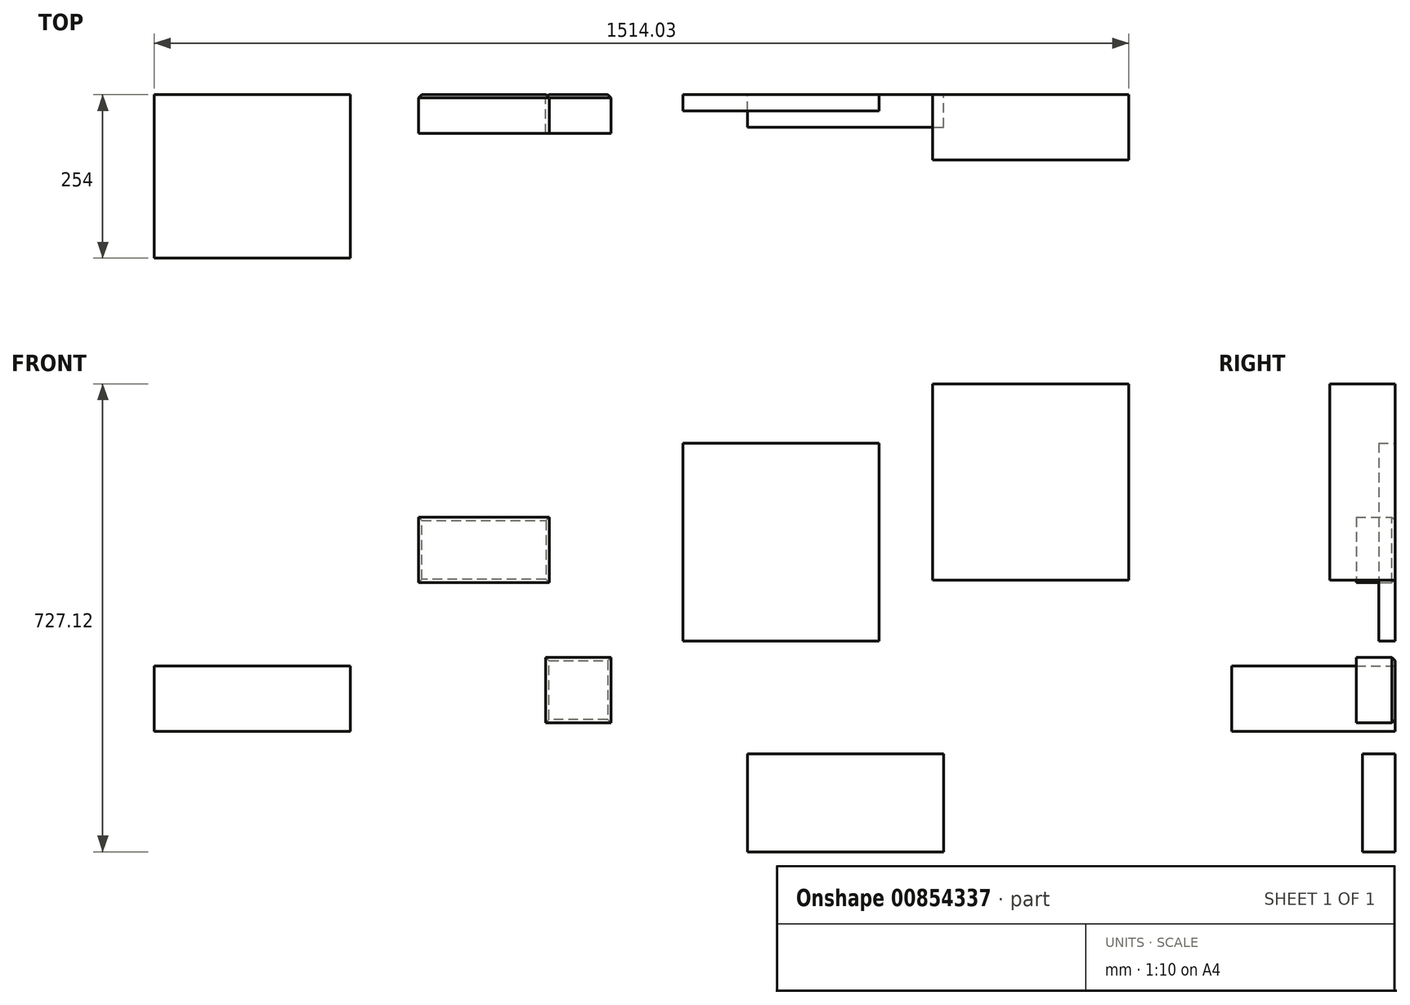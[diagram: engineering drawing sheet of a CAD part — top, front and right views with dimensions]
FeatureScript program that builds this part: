
annotation { "Feature Type Name" : "Feature", "Feature Type Description" : "" }
export const myFeature = defineFeature(function(context is Context, id is Id, definition is map)
    precondition{}
    {
        {
            var Q0;
            Q0=qCreatedBy(makeId("Front.planeOp"),FACE);
            var sketch = newSketch(context, id + "F0", { "sketchPlane" : qUnion([Q0])});
            skLineSegment(sketch, "E0.bottom", {"start": v(-238.03, 40.6) * mm, "end": v(-34.83, 40.6) * mm});
            skLineSegment(sketch, "E0.top", {"start": v(-238.03, -61) * mm, "end": v(-34.83, -61) * mm});
            skLineSegment(sketch, "E0.left", {"start": v(-238.03, 40.6) * mm, "end": v(-238.03, -61) * mm});
            skLineSegment(sketch, "E0.right", {"start": v(-34.83, 40.6) * mm, "end": v(-34.83, -61) * mm});
            skLineSegment(sketch, "E1.bottom", {"start": v(-238.03, 40.6) * mm, "end": v(-339.63, 40.6) * mm});
            skLineSegment(sketch, "E1.top", {"start": v(-238.03, -162.6) * mm, "end": v(-339.63, -162.6) * mm});
            skLineSegment(sketch, "E1.left", {"start": v(-238.03, 40.6) * mm, "end": v(-238.03, -162.6) * mm});
            skLineSegment(sketch, "E1.right", {"start": v(-339.63, 40.6) * mm, "end": v(-339.63, -162.6) * mm});
            skLineSegment(sketch, "E2.bottom", {"start": v(-238.03, -61) * mm, "end": v(-135.35, -61) * mm});
            skLineSegment(sketch, "E2.top", {"start": v(-238.03, -252.07) * mm, "end": v(-135.35, -252.07) * mm});
            skLineSegment(sketch, "E2.left", {"start": v(-238.03, -61) * mm, "end": v(-238.03, -252.07) * mm});
            skLineSegment(sketch, "E2.right", {"start": v(-135.35, -61) * mm, "end": v(-135.35, -252.07) * mm});
            skSolve(sketch);
        }
        {
            var Q0;
            Q0=makeQuery(id+"F0.imprint","IMPRINT",FACE,{"disambiguationData":[TD([[makeQuery(id+"F0.imprint","IMPRINT",EDGE,{"derivedFrom":sQuery(id+"F0.wireOp",EDGE,"E0.bottom")}),-1.0]])]});
            extrude(context, id + "F1", {"entities" : qUnion([Q0]), "depth" : 60.32 * mm, "offsetDistance" : 25.4 * mm});
        }
        {
            var Q0;
            Q0=makeQuery(id+"F1.opExtrude","CAP_EDGE",EDGE,{"disambiguationData":[OSD([sQuery(id+"F0.wireOp",EDGE,"E0.top")])],"isStart":true});
            var Q1;
            Q1=makeQuery(id+"F1.opExtrude","CAP_EDGE",EDGE,{"disambiguationData":[OSD([sQuery(id+"F0.wireOp",EDGE,"E0.left")])],"isStart":true});
            var Q2;
            Q2=makeQuery(id+"F1.opExtrude","CAP_EDGE",EDGE,{"disambiguationData":[OSD([sQuery(id+"F0.wireOp",EDGE,"E0.bottom")])],"isStart":true});
            var Q3;
            Q3=makeQuery(id+"F1.opExtrude","CAP_EDGE",EDGE,{"disambiguationData":[OSD([sQuery(id+"F0.wireOp",EDGE,"E0.right")])],"isStart":true});
            chamfer(context, id + "F2", {"entities" : qUnion([Q0, Q1, Q2, Q3]), "width" : 5.08 * mm, "tangentPropagation" : true});
        }
        {
            var Q0;
            Q0=qCreatedBy(makeId("Front.planeOp"),FACE);
            var sketch = newSketch(context, id + "F3", { "sketchPlane" : qUnion([Q0])});
            skLineSegment(sketch, "E3.bottom", {"start": v(172.78, 155.68) * mm, "end": v(477.58, 155.68) * mm});
            skLineSegment(sketch, "E3.top", {"start": v(172.78, -151.77) * mm, "end": v(477.58, -151.77) * mm});
            skLineSegment(sketch, "E3.left", {"start": v(172.78, 155.68) * mm, "end": v(172.78, -151.77) * mm});
            skLineSegment(sketch, "E3.right", {"start": v(477.58, 155.68) * mm, "end": v(477.58, -151.77) * mm});
            skSolve(sketch);
        }
        {
            var Q0;
            Q0=makeQuery(id+"F3.imprint","IMPRINT",FACE,{"disambiguationData":[TD([[makeQuery(id+"F3.imprint","IMPRINT",EDGE,{"derivedFrom":sQuery(id+"F3.wireOp",EDGE,"E3.bottom")}),-1.0]])]});
            extrude(context, id + "F4", {"entities" : qUnion([Q0]), "depth" : 25.4 * mm, "offsetDistance" : 25.4 * mm});
        }
        {
            var Q0;
            Q0=qCreatedBy(makeId("Front.planeOp"),FACE);
            var sketch = newSketch(context, id + "F5", { "sketchPlane" : qUnion([Q0])});
            skLineSegment(sketch, "E4.bottom", {"start": v(560.75, 247.93) * mm, "end": v(865.55, 247.93) * mm});
            skLineSegment(sketch, "E4.top", {"start": v(560.75, -56.87) * mm, "end": v(865.55, -56.87) * mm});
            skLineSegment(sketch, "E4.left", {"start": v(560.75, 247.93) * mm, "end": v(560.75, -56.87) * mm});
            skLineSegment(sketch, "E4.right", {"start": v(865.55, 247.93) * mm, "end": v(865.55, -56.87) * mm});
            skSolve(sketch);
        }
        {
            var Q0;
            Q0=makeQuery(id+"F5.imprint","IMPRINT",FACE,{"disambiguationData":[TD([[makeQuery(id+"F5.imprint","IMPRINT",EDGE,{"derivedFrom":sQuery(id+"F5.wireOp",EDGE,"E4.bottom")}),-1.0]])]});
            extrude(context, id + "F6", {"entities" : qUnion([Q0]), "depth" : 101.6 * mm, "offsetDistance" : 25.4 * mm});
        }
        {
            var Q0;
            Q0=qCreatedBy(makeId("Front.planeOp"),FACE);
            var sketch = newSketch(context, id + "F7", { "sketchPlane" : qUnion([Q0])});
            skLineSegment(sketch, "E5.bottom", {"start": v(-40.4, -278.66) * mm, "end": v(61.2, -278.66) * mm});
            skLineSegment(sketch, "E5.top", {"start": v(-40.4, -177.06) * mm, "end": v(61.2, -177.06) * mm});
            skLineSegment(sketch, "E5.left", {"start": v(-40.4, -278.66) * mm, "end": v(-40.4, -177.06) * mm});
            skLineSegment(sketch, "E5.right", {"start": v(61.2, -278.66) * mm, "end": v(61.2, -177.06) * mm});
            skSolve(sketch);
        }
        {
            var Q0;
            Q0=makeQuery(id+"F7.imprint","IMPRINT",FACE,{"disambiguationData":[TD([[makeQuery(id+"F7.imprint","IMPRINT",EDGE,{"derivedFrom":sQuery(id+"F7.wireOp",EDGE,"E5.bottom")}),1.0]])]});
            extrude(context, id + "F8", {"entities" : qUnion([Q0]), "depth" : 60.32 * mm, "offsetDistance" : 25.4 * mm});
        }
        {
            var Q0;
            Q0=makeQuery(id+"F8.opExtrude","CAP_EDGE",EDGE,{"disambiguationData":[OSD([sQuery(id+"F7.wireOp",EDGE,"E5.right")])],"isStart":true});
            var Q1;
            Q1=makeQuery(id+"F8.opExtrude","CAP_EDGE",EDGE,{"disambiguationData":[OSD([sQuery(id+"F7.wireOp",EDGE,"E5.bottom")])],"isStart":true});
            var Q2;
            Q2=makeQuery(id+"F8.opExtrude","CAP_EDGE",EDGE,{"disambiguationData":[OSD([sQuery(id+"F7.wireOp",EDGE,"E5.left")])],"isStart":true});
            var Q3;
            Q3=makeQuery(id+"F8.opExtrude","CAP_EDGE",EDGE,{"disambiguationData":[OSD([sQuery(id+"F7.wireOp",EDGE,"E5.top")])],"isStart":true});
            chamfer(context, id + "F9", {"entities" : qUnion([Q0, Q1, Q2, Q3]), "width" : 5.08 * mm, "tangentPropagation" : true});
        }
        {
            var Q0;
            Q0=qCreatedBy(makeId("Front.planeOp"),FACE);
            var sketch = newSketch(context, id + "F10", { "sketchPlane" : qUnion([Q0])});
            skLineSegment(sketch, "E6.bottom", {"start": v(273.1, -326.8) * mm, "end": v(577.9, -326.8) * mm});
            skLineSegment(sketch, "E6.top", {"start": v(273.1, -479.2) * mm, "end": v(577.9, -479.2) * mm});
            skLineSegment(sketch, "E6.left", {"start": v(273.1, -326.8) * mm, "end": v(273.1, -479.2) * mm});
            skLineSegment(sketch, "E6.right", {"start": v(577.9, -326.8) * mm, "end": v(577.9, -479.2) * mm});
            skSolve(sketch);
        }
        {
            var Q0;
            Q0=makeQuery(id+"F10.imprint","IMPRINT",FACE,{"disambiguationData":[TD([[makeQuery(id+"F10.imprint","IMPRINT",EDGE,{"derivedFrom":sQuery(id+"F10.wireOp",EDGE,"E6.bottom")}),-1.0]])]});
            extrude(context, id + "F11", {"entities" : qUnion([Q0]), "depth" : 50.8 * mm, "offsetDistance" : 25.4 * mm});
        }
        {
            var Q0;
            Q0=qCreatedBy(makeId("Front.planeOp"),FACE);
            var sketch = newSketch(context, id + "F12", { "sketchPlane" : qUnion([Q0])});
            skLineSegment(sketch, "E7.bottom", {"start": v(-343.68, -291.9) * mm, "end": v(-648.48, -291.9) * mm});
            skLineSegment(sketch, "E7.top", {"start": v(-343.68, -190.3) * mm, "end": v(-648.48, -190.3) * mm});
            skLineSegment(sketch, "E7.left", {"start": v(-343.68, -291.9) * mm, "end": v(-343.68, -190.3) * mm});
            skLineSegment(sketch, "E7.right", {"start": v(-648.48, -291.9) * mm, "end": v(-648.48, -190.3) * mm});
            skSolve(sketch);
        }
        {
            var Q0;
            Q0=makeQuery(id+"F12.imprint","IMPRINT",FACE,{"disambiguationData":[TD([[makeQuery(id+"F12.imprint","IMPRINT",EDGE,{"derivedFrom":sQuery(id+"F12.wireOp",EDGE,"E7.bottom")}),-1.0]])]});
            extrude(context, id + "F13", {"entities" : qUnion([Q0]), "depth" : 254 * mm, "offsetDistance" : 25.4 * mm});
        }
    });
